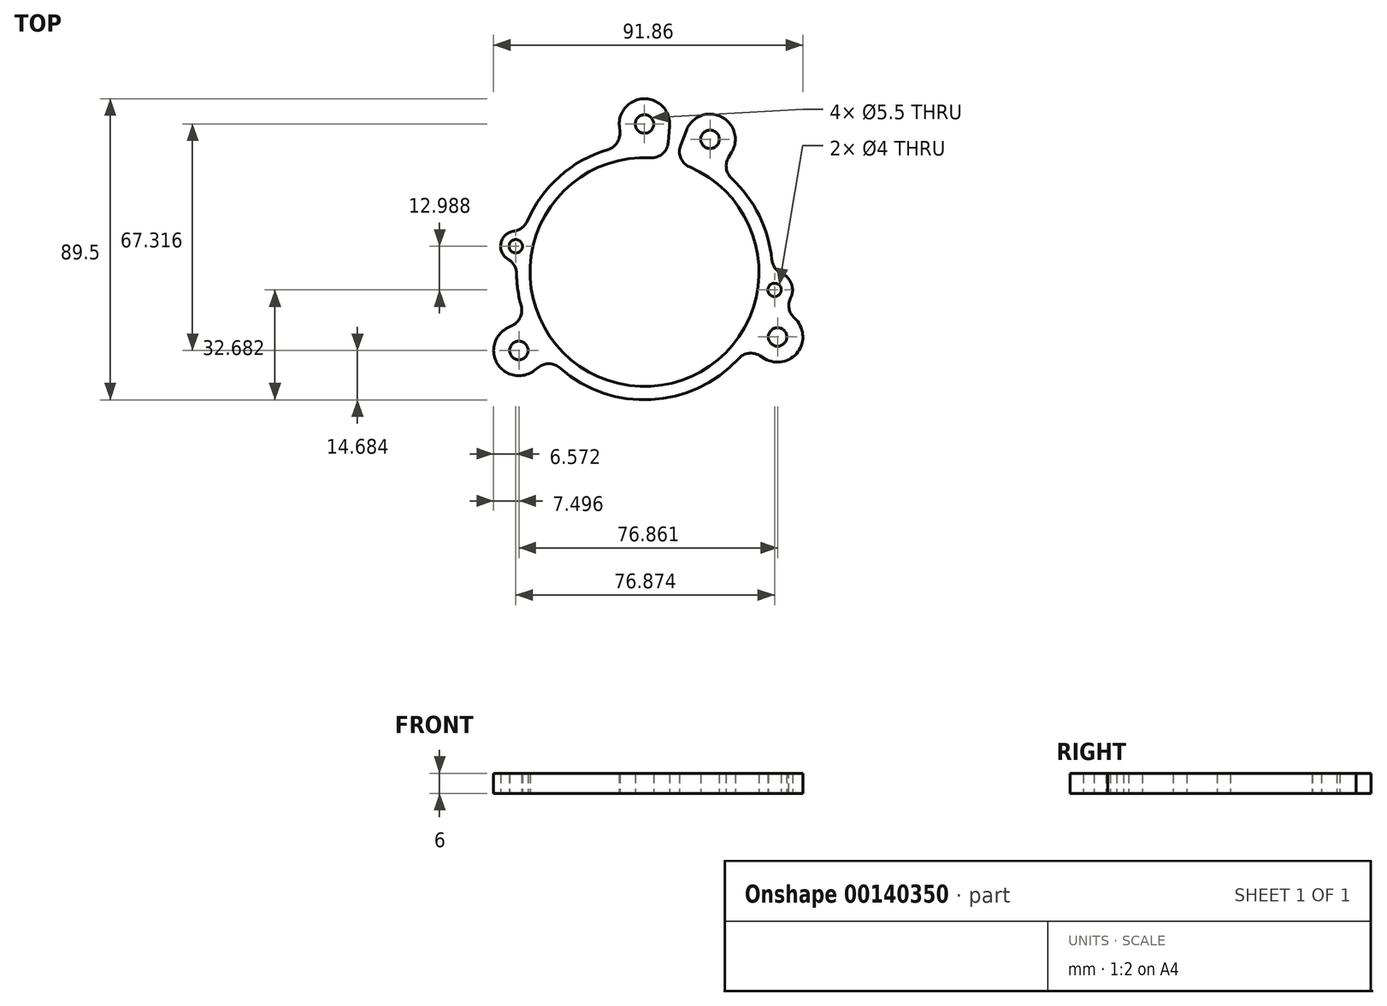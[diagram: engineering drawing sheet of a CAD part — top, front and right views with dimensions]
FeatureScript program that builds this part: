
annotation { "Feature Type Name" : "Feature", "Feature Type Description" : "" }
export const myFeature = defineFeature(function(context is Context, id is Id, definition is map)
    precondition{}
    {
        {
            var Q0;
            Q0=qCreatedBy(makeId("Top.planeOp"),FACE);
            var sketch = newSketch(context, id + "F0", { "sketchPlane" : qUnion([Q0])});
            skArc(sketch, "E0", {"start": v(6.62, 33.35) * mm, "mid": v(-7.73, -33.11) * mm, "end": v(8.83, 32.83) * mm});
            skArc(sketch, "E1", {"start": v(-6.96, 37.36) * mm, "mid": v(-25.1, 28.53) * mm, "end": v(-36.17, 11.66) * mm});
            skLineSegment(sketch, "E2", {"start": v(0, 0) * mm, "end": v(45, -21.94) * mm, "construction": true});
            skLineSegment(sketch, "E3", {"start": v(0, 0) * mm, "end": v(-44.09, -27.55) * mm, "construction": true});
            skCircle(sketch, "E4", {"center": v(0, 0) * mm, "radius": 44 * mm, "construction": true});
            skPoint(sketch, "E5", {"position": v(-37.31, -23.32) * mm});
            skPoint(sketch, "E6", {"position": v(39.55, -19.29) * mm});
            skPoint(sketch, "E7", {"position": v(0, 44) * mm});
            skPoint(sketch, "E8", {"position": v(19.48, 39.45) * mm});
            skArc(sketch, "E9", {"start": v(7.47, 43.36) * mm, "mid": v(0, 51.5) * mm, "end": v(-7.47, 43.36) * mm});
            skArc(sketch, "E10", {"start": v(25.9, 35.57) * mm, "mid": v(22.8, 46.18) * mm, "end": v(12.5, 42.19) * mm});
            skArc(sketch, "E11", {"start": v(35.7, -25.72) * mm, "mid": v(46.29, -22.58) * mm, "end": v(42.25, -12.3) * mm});
            skArc(sketch, "E12", {"start": v(-40.73, -16.64) * mm, "mid": v(-43.67, -27.3) * mm, "end": v(-32.81, -29.31) * mm});
            skLineSegment(sketch, "E13", {"start": v(-40.73, -16.64) * mm, "end": v(-35.37, -13.9) * mm});
            skLineSegment(sketch, "E14", {"start": v(-32.81, -29.31) * mm, "end": v(-28, -25.7) * mm});
            skLineSegment(sketch, "E15", {"start": v(7.47, 43.36) * mm, "end": v(6.96, 37.36) * mm});
            skLineSegment(sketch, "E16", {"start": v(-7.47, 43.36) * mm, "end": v(-6.96, 37.36) * mm});
            skLineSegment(sketch, "E17", {"start": v(12.5, 42.19) * mm, "end": v(10.3, 36.58) * mm});
            skLineSegment(sketch, "E18", {"start": v(25.9, 35.57) * mm, "end": v(22.78, 30.42) * mm});
            skLineSegment(sketch, "E19", {"start": v(42.25, -12.3) * mm, "end": v(37.87, -10.6) * mm});
            skLineSegment(sketch, "E20", {"start": v(35.7, -25.72) * mm, "end": v(30.53, -22.63) * mm});
            skLineSegment(sketch, "E21", {"start": v(6.96, 37.36) * mm, "end": v(6.62, 33.35) * mm});
            skLineSegment(sketch, "E22", {"start": v(10.3, 36.58) * mm, "end": v(8.83, 32.83) * mm});
            skArc(sketch, "E23.trimOffspring", {"start": v(38, -0.02) * mm, "mid": v(33.99, 17) * mm, "end": v(22.78, 30.42) * mm});
            skCircle(sketch, "E24", {"center": v(0, 0) * mm, "radius": 39 * mm, "construction": true});
            skPoint(sketch, "E25", {"position": v(38.64, -5.32) * mm});
            skPoint(sketch, "E26", {"position": v(-38.24, 7.67) * mm});
            skArc(sketch, "E27", {"start": v(-36.17, 11.66) * mm, "mid": v(-42.65, 8.55) * mm, "end": v(-37.87, 3.19) * mm});
            skArc(sketch, "E28.trimOffspring", {"start": v(-37.87, 3.19) * mm, "mid": v(-37.6, -5.5) * mm, "end": v(-35.37, -13.9) * mm});
            skArc(sketch, "E29.trimOffspring", {"start": v(-28, -25.7) * mm, "mid": v(1.99, -37.95) * mm, "end": v(30.53, -22.63) * mm});
            skLineSegment(sketch, "E30", {"start": v(33.4, -6.36) * mm, "end": v(33.4, -6.36) * mm});
            skArc(sketch, "E31.trimOffspring", {"start": v(37.87, -10.6) * mm, "mid": v(43.97, -5.38) * mm, "end": v(38, -0.02) * mm});
            skSolve(sketch);
        }
        {
            var Q0;
            Q0=makeQuery(id+"F0.imprint","IMPRINT",FACE,{"disambiguationData":[TD([[makeQuery(id+"F0.imprint","IMPRINT",EDGE,{"derivedFrom":sQuery(id+"F0.wireOp",EDGE,"E0")}),-1.0]])]});
            extrude(context, id + "F1", {"entities" : qUnion([Q0]), "depth" : 6 * mm});
        }
        {
            var Q0;
            Q0=makeQuery(id+"F1.opExtrude","SWEPT_EDGE",EDGE,{"disambiguationData":[OSD([sQuery(id+"F0.wireOp",EDGE,"E1"),sQuery(id+"F0.wireOp",EDGE,"E16")])]});
            var Q1;
            Q1=makeQuery(id+"F1.opExtrude","SWEPT_EDGE",EDGE,{"disambiguationData":[OSD([sQuery(id+"F0.wireOp",EDGE,"E1"),sQuery(id+"F0.wireOp",EDGE,"E27")])]});
            var Q2;
            Q2=makeQuery(id+"F1.opExtrude","SWEPT_EDGE",EDGE,{"disambiguationData":[OSD([sQuery(id+"F0.wireOp",EDGE,"E13"),sQuery(id+"F0.wireOp",EDGE,"E28.trimOffspring")])]});
            var Q3;
            Q3=makeQuery(id+"F1.opExtrude","SWEPT_EDGE",EDGE,{"disambiguationData":[OSD([sQuery(id+"F0.wireOp",EDGE,"E27"),sQuery(id+"F0.wireOp",EDGE,"E28.trimOffspring")])]});
            var Q4;
            Q4=makeQuery(id+"F1.opExtrude","SWEPT_EDGE",EDGE,{"disambiguationData":[OSD([sQuery(id+"F0.wireOp",EDGE,"E14"),sQuery(id+"F0.wireOp",EDGE,"E29.trimOffspring")])]});
            var Q5;
            Q5=makeQuery(id+"F1.opExtrude","SWEPT_EDGE",EDGE,{"disambiguationData":[OSD([sQuery(id+"F0.wireOp",EDGE,"E20"),sQuery(id+"F0.wireOp",EDGE,"E29.trimOffspring")])]});
            var Q6;
            Q6=makeQuery(id+"F1.opExtrude","SWEPT_EDGE",EDGE,{"disambiguationData":[OSD([sQuery(id+"F0.wireOp",EDGE,"E23.trimOffspring"),sQuery(id+"F0.wireOp",EDGE,"f69FU7yq-HSvo-iqtR-TdjN-gZaDXmuuRK0c")])]});
            var Q7;
            Q7=makeQuery(id+"F1.opExtrude","SWEPT_EDGE",EDGE,{"disambiguationData":[OSD([sQuery(id+"F0.wireOp",EDGE,"E18"),sQuery(id+"F0.wireOp",EDGE,"E23.trimOffspring")])]});
            var Q8;
            Q8=makeQuery(id+"F1.opExtrude","SWEPT_EDGE",EDGE,{"disambiguationData":[OSD([sQuery(id+"F0.wireOp",EDGE,"E19"),sQuery(id+"F0.wireOp",EDGE,"f69FU7yq-HSvo-iqtR-TdjN-gZaDXmuuRK0c")])]});
            var Q9;
            Q9=makeQuery(id+"F1.opExtrude","SWEPT_EDGE",EDGE,{"disambiguationData":[OSD([sQuery(id+"F0.wireOp",EDGE,"E0"),sQuery(id+"F0.wireOp",EDGE,"E22")])]});
            var Q10;
            Q10=makeQuery(id+"F1.opExtrude","SWEPT_EDGE",EDGE,{"disambiguationData":[OSD([sQuery(id+"F0.wireOp",EDGE,"E0"),sQuery(id+"F0.wireOp",EDGE,"E21")])]});
            fillet(context, id + "F2", {"entities" : qUnion([Q0, Q1, Q2, Q3, Q4, Q5, Q6, Q7, Q8, Q9, Q10]), "radius" : 5 * mm, "tangentPropagation" : true, "allowEdgeOverflow" : false});
        }
        {
            var Q0;
            Q0=sQuery(id+"F0.wireOp",VERTEX,"E7");
            var Q1;
            Q1=sQuery(id+"F0.wireOp",VERTEX,"E8");
            var Q2;
            Q2=sQuery(id+"F0.wireOp",VERTEX,"E5");
            var Q3;
            Q3=sQuery(id+"F0.wireOp",VERTEX,"E6");
            var Q4;
            Q4=makeQuery(id+"F1.opExtrude","SWEPT_BODY",BODY,{"disambiguationData":[OSD([sQuery(id+"F0.wireOp",EDGE,"E0"),sQuery(id+"F0.wireOp",EDGE,"E1"),sQuery(id+"F0.wireOp",EDGE,"E9"),sQuery(id+"F0.wireOp",EDGE,"E10"),sQuery(id+"F0.wireOp",EDGE,"E11"),sQuery(id+"F0.wireOp",EDGE,"E12"),sQuery(id+"F0.wireOp",EDGE,"E13"),sQuery(id+"F0.wireOp",EDGE,"E14"),sQuery(id+"F0.wireOp",EDGE,"E15"),sQuery(id+"F0.wireOp",EDGE,"E16"),sQuery(id+"F0.wireOp",EDGE,"E17"),sQuery(id+"F0.wireOp",EDGE,"E18"),sQuery(id+"F0.wireOp",EDGE,"E19"),sQuery(id+"F0.wireOp",EDGE,"E20"),sQuery(id+"F0.wireOp",EDGE,"E21"),sQuery(id+"F0.wireOp",EDGE,"E22"),sQuery(id+"F0.wireOp",EDGE,"E23.trimOffspring"),sQuery(id+"F0.wireOp",EDGE,"E27"),sQuery(id+"F0.wireOp",EDGE,"f69FU7yq-HSvo-iqtR-TdjN-gZaDXmuuRK0c"),sQuery(id+"F0.wireOp",EDGE,"E28.trimOffspring"),sQuery(id+"F0.wireOp",EDGE,"E29.trimOffspring")])]});
            hole(context, id + "F3", {"style" : HoleStyle.SIMPLE, "endStyle" : HoleEndStyle.THROUGH, "oppositeDirection" : true, "holeDiameter" : 5.5 * mm, "startFromSketch" : true, "locations" : qUnion([Q0, Q1, Q2, Q3]), "scope" : qUnion([Q4]), "isTappedThrough" : true});
        }
        {
            var Q0;
            Q0=sQuery(id+"F0.wireOp",VERTEX,"E25");
            var Q1;
            Q1=sQuery(id+"F0.wireOp",VERTEX,"E26");
            var Q2;
            Q2=makeQuery(id+"F1.opExtrude","SWEPT_BODY",BODY,{"disambiguationData":[OSD([sQuery(id+"F0.wireOp",EDGE,"E0"),sQuery(id+"F0.wireOp",EDGE,"E1"),sQuery(id+"F0.wireOp",EDGE,"E9"),sQuery(id+"F0.wireOp",EDGE,"E10"),sQuery(id+"F0.wireOp",EDGE,"E11"),sQuery(id+"F0.wireOp",EDGE,"E12"),sQuery(id+"F0.wireOp",EDGE,"E13"),sQuery(id+"F0.wireOp",EDGE,"E14"),sQuery(id+"F0.wireOp",EDGE,"E15"),sQuery(id+"F0.wireOp",EDGE,"E16"),sQuery(id+"F0.wireOp",EDGE,"E17"),sQuery(id+"F0.wireOp",EDGE,"E18"),sQuery(id+"F0.wireOp",EDGE,"E19"),sQuery(id+"F0.wireOp",EDGE,"E20"),sQuery(id+"F0.wireOp",EDGE,"E21"),sQuery(id+"F0.wireOp",EDGE,"E22"),sQuery(id+"F0.wireOp",EDGE,"E23.trimOffspring"),sQuery(id+"F0.wireOp",EDGE,"E27"),sQuery(id+"F0.wireOp",EDGE,"f69FU7yq-HSvo-iqtR-TdjN-gZaDXmuuRK0c"),sQuery(id+"F0.wireOp",EDGE,"E28.trimOffspring"),sQuery(id+"F0.wireOp",EDGE,"E29.trimOffspring")])]});
            hole(context, id + "F4", {"style" : HoleStyle.SIMPLE, "endStyle" : HoleEndStyle.THROUGH, "oppositeDirection" : true, "holeDiameter" : 4 * mm, "startFromSketch" : true, "locations" : qUnion([Q0, Q1]), "scope" : qUnion([Q2]), "isTappedThrough" : true});
        }
    });
